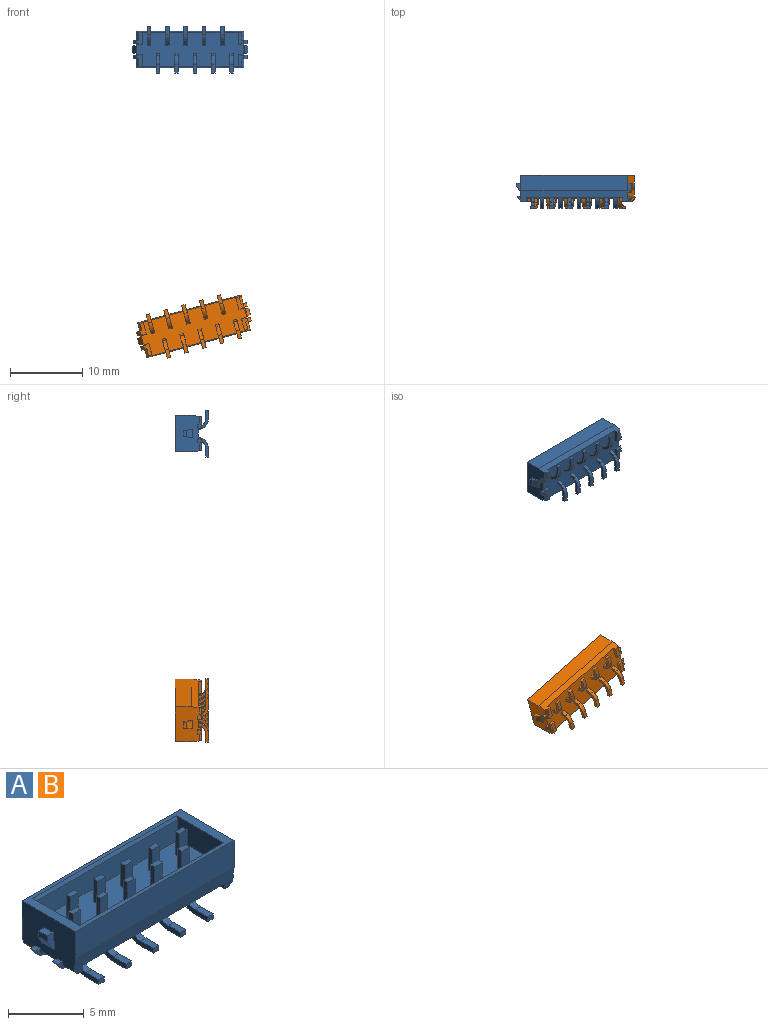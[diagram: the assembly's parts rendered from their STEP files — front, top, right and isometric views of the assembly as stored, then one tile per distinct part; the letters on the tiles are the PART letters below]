
ASSEMBLY  parts=2 mates=1
PART A: 227 faces, bbox 15.9x6.5x4.6 mm
  f0: plane 5x3.3mm, normal (-1,0,0), area 14.7mm2, adj f1,f3,f5,f6,f7,f8,f11,f14
  f1: plane 1.25x0.55mm, normal (0,0.99,0.12), area 0.5mm2, adj f0,f2,f4,f5,f6
  f2: plane 1.11x0.78mm, normal (-0.87,0,-0.5), area 0.9mm2, adj f1,f3,f4,f6
  f3: plane 1.25x0.55mm, normal (0,-0.99,0.12), area 0.5mm2, adj f0,f2,f4,f5,f6
  f4: plane 0.92x0.47mm, normal (-1,0,0), area 0.4mm2, adj f1,f2,f3,f5
  f5: plane 0.8x0.55mm, normal (0,0,1), area 0.4mm2, adj f0,f1,f3,f4
  f6: plane 1.11x0.1mm, normal (0,0,-1), area 0.1mm2, adj f0,f1,f2,f3
  f7: plane 0.5x0.45mm, normal (0,0,1), area 0.2mm2, adj f0,f11,f45,f46
  f8: plane 0.5x0.45mm, normal (0,0,1), area 0.2mm2, adj f0,f14,f112,f113
  f9: plane 0.5x0.45mm, normal (0,0,1), area 0.2mm2, adj f28,f224,f225,f226
  f10: plane 0.5x0.45mm, normal (0,0,1), area 0.2mm2, adj f21,f22,f23,f28
  f11: plane 0.75x0.6mm, normal (0,-1,0), area 0.2mm2, adj f0,f7,f13,f18,f41,f46
  f12: plane 0.54x0.5mm, normal (-0.77,0,-0.64), area 0.4mm2, adj f14,f17,f112,f113
  f13: plane 0.54x0.5mm, normal (-0.77,0,-0.64), area 0.4mm2, adj f11,f18,f45,f46
  f14: plane 0.75x0.6mm, normal (0,1,0), area 0.2mm2, adj f0,f8,f12,f17,f44,f113
  f15: plane 1.68x0.78mm, normal (0,0,-1), area 0.9mm2, adj f19,f21,f23,f24,f25,f35,f48,f51
  f16: plane 1.68x0.78mm, normal (0,0,-1), area 0.9mm2, adj f20,f26,f27,f40,f47,f49,f224,f226
  f17: plane 1.68x0.78mm, normal (0,0,-1), area 0.9mm2, adj f12,f14,f35,f36,f43,f44,f50,f112
  f18: plane 1.68x0.78mm, normal (0,0,-1), area 0.9mm2, adj f11,f13,f37,f39,f41,f42,f45,f47
  f19: plane 0.54x0.5mm, normal (0.77,0,-0.64), area 0.4mm2, adj f15,f21,f22,f23
  f20: plane 0.54x0.5mm, normal (0.77,0,-0.64), area 0.4mm2, adj f16,f224,f225,f226
  f21: plane 0.75x0.6mm, normal (0,1,0), area 0.2mm2, adj f10,f15,f19,f22,f24,f28
  f22: plane 0.5x0.06mm, normal (1,0,0), area 0mm2, adj f10,f19,f21,f23
  f23: plane 0.75x0.6mm, normal (0,-1,0), area 0.2mm2, adj f10,f15,f19,f22,f25,f28
  f24: plane 0.3x0.3mm, normal (0.71,0,-0.71), area 0.1mm2, adj f15,f21,f28,f51
  f25: plane 1.08x0.3mm, normal (0.71,0,-0.71), area 0.5mm2, adj f15,f23,f28,f35
  f26: plane 1.08x0.3mm, normal (0.71,0,-0.71), area 0.5mm2, adj f16,f28,f47,f224
  f27: plane 0.3x0.3mm, normal (0.71,0,-0.71), area 0.1mm2, adj f16,f28,f40,f226
  f28: plane 5x3.3mm, normal (1,0,0), area 14.7mm2, adj f9,f10,f21,f23,f24,f25,f26,f27
  f29: plane 1.25x0.55mm, normal (0,0.99,0.12), area 0.5mm2, adj f28,f30,f31,f33,f34
  f30: plane 1.11x0.78mm, normal (0.87,0,-0.5), area 0.9mm2, adj f29,f31,f32,f34
  f31: plane 1.11x0.1mm, normal (0,0,-1), area 0.1mm2, adj f28,f29,f30,f32
  f32: plane 1.25x0.55mm, normal (0,-0.99,0.12), area 0.5mm2, adj f28,f30,f31,f33,f34
  f33: plane 0.8x0.55mm, normal (0,0,1), area 0.4mm2, adj f28,f29,f32,f34
  f34: plane 0.92x0.47mm, normal (1,0,0), area 0.4mm2, adj f29,f30,f32,f33
  f35: plane 14.78x1.4mm, normal (0,-0.99,-0.1), area 14.7mm2, adj f0,f15,f17,f25,f28,f36,f38,f43
  f36: plane 1.73x0.45mm, normal (1,0,0), area 0.8mm2, adj f17,f35,f38,f50
  f37: plane 1.73x0.45mm, normal (1,0,0), area 0.8mm2, adj f18,f38,f39,f47
  f38: plane 14.78x4.8mm, normal (0,0,-1), area 63.6mm2, adj f0,f28,f35,f36,f37,f39,f40,f47
  f39: plane 0.78x0.45mm, normal (0,-1,0), area 0.3mm2, adj f0,f18,f37,f38,f41
  f40: plane 0.78x0.45mm, normal (0,-1,0), area 0.3mm2, adj f16,f27,f28,f38,f49
  f41: plane 0.3x0.3mm, normal (-0.71,0,-0.71), area 0.1mm2, adj f0,f11,f18,f39
  f42: plane 1.08x0.3mm, normal (-0.71,0,-0.71), area 0.5mm2, adj f0,f18,f45,f47
  f43: plane 1.08x0.3mm, normal (-0.71,0,-0.71), area 0.5mm2, adj f0,f17,f35,f112
  f44: plane 0.3x0.3mm, normal (-0.71,0,-0.71), area 0.1mm2, adj f0,f14,f17,f50
  f45: plane 0.75x0.6mm, normal (0,1,0), area 0.2mm2, adj f0,f7,f13,f18,f42,f46
  f46: plane 0.5x0.06mm, normal (-1,0,0), area 0mm2, adj f7,f11,f13,f45
  f47: plane 14.78x1.4mm, normal (0,0.99,-0.1), area 14.7mm2, adj f0,f16,f18,f26,f28,f37,f38,f42
  f48: plane 1.73x0.45mm, normal (-1,0,0), area 0.8mm2, adj f15,f35,f38,f51
  f49: plane 1.73x0.45mm, normal (-1,0,0), area 0.8mm2, adj f16,f38,f40,f47
  f50: plane 0.78x0.45mm, normal (0,1,0), area 0.3mm2, adj f0,f17,f36,f38,f44
  f51: plane 0.78x0.45mm, normal (0,1,0), area 0.3mm2, adj f15,f24,f28,f38,f48
  f52: plane 14.78x2.2mm, normal (0,1,0), area 32.5mm2, adj f0,f28,f47,f53
  f53: plane 14.78x5mm, normal (0,0,1), area 15mm2, adj f0,f28,f52,f54,f55,f58,f59,f60
  f54: plane 14.78x2.2mm, normal (0,-1,0), area 32.5mm2, adj f0,f28,f35,f53
  f55: plane 4.4x1.85mm, normal (-1,0,0), area 7.6mm2, adj f53,f56,f57,f58,f60,f61
  f56: plane 13.38x4mm, normal (0,0,1), area 50.8mm2, adj f55,f57,f59,f61,f62,f63,f64,f66
  f57: plane 13.38x1.61mm, normal (0,1,0.04), area 21.5mm2, adj f55,f56,f58,f59
  f58: plane 13.38x0.24mm, normal (0,0.87,0.5), area 3.7mm2, adj f53,f55,f57,f59
  f59: plane 4.4x1.85mm, normal (1,0,0), area 7.6mm2, adj f53,f56,f57,f58,f60,f61
  f60: plane 13.38x0.24mm, normal (0,-0.87,0.5), area 3.7mm2, adj f53,f55,f59,f61
  f61: plane 13.38x1.61mm, normal (0,-1,0.04), area 21.5mm2, adj f55,f56,f59,f60
  f62: plane 1.85x0.7mm, normal (0,1,0), area 1.3mm2, adj f56,f63,f65,f66
  f63: plane 1.85x0.39mm, normal (1,0,0), area 0.7mm2, adj f56,f62,f64,f65
  f64: plane 1.85x0.7mm, normal (0,-1,0), area 1.3mm2, adj f56,f63,f65,f66
  f65: plane 0.7x0.39mm, normal (0,0,1), area 0.3mm2, adj f62,f63,f64,f66
  f66: plane 1.85x0.39mm, normal (-1,0,0), area 0.7mm2, adj f56,f62,f64,f65
  f67: plane 1.85x0.7mm, normal (0,-1,0), area 1.3mm2, adj f56,f68,f70,f71
  f68: plane 1.85x0.39mm, normal (-1,0,0), area 0.7mm2, adj f56,f67,f69,f70
  f69: plane 1.85x0.7mm, normal (0,1,0), area 1.3mm2, adj f56,f68,f70,f71
  f70: plane 0.7x0.39mm, normal (0,0,1), area 0.3mm2, adj f67,f68,f69,f71
  f71: plane 1.85x0.39mm, normal (1,0,0), area 0.7mm2, adj f56,f67,f69,f70
  f72: plane 1.85x0.7mm, normal (0,1,0), area 1.3mm2, adj f56,f73,f75,f76
  f73: plane 1.85x0.39mm, normal (1,0,0), area 0.7mm2, adj f56,f72,f74,f75
  f74: plane 1.85x0.7mm, normal (0,-1,0), area 1.3mm2, adj f56,f73,f75,f76
  f75: plane 0.7x0.39mm, normal (0,0,1), area 0.3mm2, adj f72,f73,f74,f76
  f76: plane 1.85x0.39mm, normal (-1,0,0), area 0.7mm2, adj f56,f72,f74,f75
  f77: plane 1.85x0.7mm, normal (0,-1,0), area 1.3mm2, adj f56,f78,f80,f81
  f78: plane 1.85x0.39mm, normal (-1,0,0), area 0.7mm2, adj f56,f77,f79,f80
  f79: plane 1.85x0.7mm, normal (0,1,0), area 1.3mm2, adj f56,f78,f80,f81
  f80: plane 0.7x0.39mm, normal (0,0,1), area 0.3mm2, adj f77,f78,f79,f81
  f81: plane 1.85x0.39mm, normal (1,0,0), area 0.7mm2, adj f56,f77,f79,f80
  f82: plane 1.85x0.7mm, normal (0,1,0), area 1.3mm2, adj f56,f83,f85,f86
  f83: plane 1.85x0.39mm, normal (1,0,0), area 0.7mm2, adj f56,f82,f84,f85
  f84: plane 1.85x0.7mm, normal (0,-1,0), area 1.3mm2, adj f56,f83,f85,f86
  f85: plane 0.7x0.39mm, normal (0,0,1), area 0.3mm2, adj f82,f83,f84,f86
  f86: plane 1.85x0.39mm, normal (-1,0,0), area 0.7mm2, adj f56,f82,f84,f85
  f87: plane 1.85x0.7mm, normal (0,-1,0), area 1.3mm2, adj f56,f88,f90,f91
  f88: plane 1.85x0.39mm, normal (-1,0,0), area 0.7mm2, adj f56,f87,f89,f90
  f89: plane 1.85x0.7mm, normal (0,1,0), area 1.3mm2, adj f56,f88,f90,f91
  f90: plane 0.7x0.39mm, normal (0,0,1), area 0.3mm2, adj f87,f88,f89,f91
  f91: plane 1.85x0.39mm, normal (1,0,0), area 0.7mm2, adj f56,f87,f89,f90
  f92: plane 1.85x0.7mm, normal (0,1,0), area 1.3mm2, adj f56,f93,f95,f96
  f93: plane 1.85x0.39mm, normal (1,0,0), area 0.7mm2, adj f56,f92,f94,f95
  f94: plane 1.85x0.7mm, normal (0,-1,0), area 1.3mm2, adj f56,f93,f95,f96
  f95: plane 0.7x0.39mm, normal (0,0,1), area 0.3mm2, adj f92,f93,f94,f96
  f96: plane 1.85x0.39mm, normal (-1,0,0), area 0.7mm2, adj f56,f92,f94,f95
  f97: plane 1.85x0.7mm, normal (0,-1,0), area 1.3mm2, adj f56,f98,f100,f101
  f98: plane 1.85x0.39mm, normal (-1,0,0), area 0.7mm2, adj f56,f97,f99,f100
  f99: plane 1.85x0.7mm, normal (0,1,0), area 1.3mm2, adj f56,f98,f100,f101
  f100: plane 0.7x0.39mm, normal (0,0,1), area 0.3mm2, adj f97,f98,f99,f101
  f101: plane 1.85x0.39mm, normal (1,0,0), area 0.7mm2, adj f56,f97,f99,f100
  f102: plane 1.85x0.7mm, normal (0,1,0), area 1.3mm2, adj f56,f103,f105,f106
  f103: plane 1.85x0.39mm, normal (1,0,0), area 0.7mm2, adj f56,f102,f104,f105
  f104: plane 1.85x0.7mm, normal (0,-1,0), area 1.3mm2, adj f56,f103,f105,f106
  f105: plane 0.7x0.39mm, normal (0,0,1), area 0.3mm2, adj f102,f103,f104,f106
  f106: plane 1.85x0.39mm, normal (-1,0,0), area 0.7mm2, adj f56,f102,f104,f105
  f107: plane 1.85x0.7mm, normal (0,-1,0), area 1.3mm2, adj f56,f108,f110,f111
  f108: plane 1.85x0.39mm, normal (-1,0,0), area 0.7mm2, adj f56,f107,f109,f110
  f109: plane 1.85x0.7mm, normal (0,1,0), area 1.3mm2, adj f56,f108,f110,f111
  f110: plane 0.7x0.39mm, normal (0,0,1), area 0.3mm2, adj f107,f108,f109,f111
  f111: plane 1.85x0.39mm, normal (1,0,0), area 0.7mm2, adj f56,f107,f109,f110
  f112: plane 0.75x0.6mm, normal (0,-1,0), area 0.2mm2, adj f0,f8,f12,f17,f43,f113
  f113: plane 0.5x0.06mm, normal (-1,0,0), area 0mm2, adj f8,f12,f14,f112
  f114: plane 2.69x1.45mm, normal (-1,0,0), area 1.2mm2, adj f38,f115,f117,f118,f119,f120,f121,f122
  f115: cylinder r=1.5mm len=0.77mm, axis (1,0,0), area 0.4mm2, adj f38,f114,f116,f124
  f116: plane 2.69x1.45mm, normal (1,0,0), area 1.2mm2, adj f38,f115,f117,f118,f119,f120,f121,f122
  f117: cylinder r=1.11mm len=0.55mm, axis (1,0,0), area 0.3mm2, adj f38,f114,f116,f118
  f118: plane 0.5x0.04mm, normal (0,0.82,0.57), area 0mm2, adj f114,f116,f117,f119
  f119: cylinder r=1.11mm len=0.91mm, axis (1,0,0), area 0.5mm2, adj f114,f116,f118,f120
  f120: plane 1.17x0.5mm, normal (0,0,1), area 0.6mm2, adj f114,f116,f119,f121
  f121: plane 0.5x0.39mm, normal (0,1,0), area 0.2mm2, adj f114,f116,f120,f122
  f122: plane 1.17x0.5mm, normal (0,0,-1), area 0.6mm2, adj f114,f116,f121,f123
  f123: cylinder r=1.5mm len=1.23mm, axis (1,0,0), area 0.7mm2, adj f114,f116,f122,f124
  f124: plane 0.5x0.04mm, normal (0,-0.82,-0.57), area 0mm2, adj f114,f115,f116,f123
  f125: plane 2.69x1.45mm, normal (-1,0,0), area 1.2mm2, adj f38,f126,f128,f129,f130,f131,f132,f133
  f126: cylinder r=1.11mm len=0.55mm, axis (1,0,0), area 0.3mm2, adj f38,f125,f127,f135
  f127: plane 2.69x1.45mm, normal (1,0,0), area 1.2mm2, adj f38,f126,f128,f129,f130,f131,f132,f133
  f128: cylinder r=1.5mm len=0.77mm, axis (1,0,0), area 0.4mm2, adj f38,f125,f127,f129
  f129: plane 0.5x0.04mm, normal (0,0.82,-0.57), area 0mm2, adj f125,f127,f128,f130
  f130: cylinder r=1.5mm len=1.23mm, axis (1,0,0), area 0.7mm2, adj f125,f127,f129,f131
  f131: plane 1.17x0.5mm, normal (0,0,-1), area 0.6mm2, adj f125,f127,f130,f132
  f132: plane 0.5x0.39mm, normal (0,-1,0), area 0.2mm2, adj f125,f127,f131,f133
  f133: plane 1.17x0.5mm, normal (0,0,1), area 0.6mm2, adj f125,f127,f132,f134
  f134: cylinder r=1.11mm len=0.91mm, axis (1,0,0), area 0.5mm2, adj f125,f127,f133,f135
  f135: plane 0.5x0.04mm, normal (0,-0.82,0.57), area 0mm2, adj f125,f126,f127,f134
  f136: plane 2.69x1.45mm, normal (-1,0,0), area 1.2mm2, adj f38,f137,f139,f140,f141,f142,f143,f144
  f137: cylinder r=1.5mm len=0.77mm, axis (1,0,0), area 0.4mm2, adj f38,f136,f138,f146
  f138: plane 2.69x1.45mm, normal (1,0,0), area 1.2mm2, adj f38,f137,f139,f140,f141,f142,f143,f144
  f139: cylinder r=1.11mm len=0.55mm, axis (1,0,0), area 0.3mm2, adj f38,f136,f138,f140
  f140: plane 0.5x0.04mm, normal (0,0.82,0.57), area 0mm2, adj f136,f138,f139,f141
  f141: cylinder r=1.11mm len=0.91mm, axis (1,0,0), area 0.5mm2, adj f136,f138,f140,f142
  f142: plane 1.17x0.5mm, normal (0,0,1), area 0.6mm2, adj f136,f138,f141,f143
  f143: plane 0.5x0.39mm, normal (0,1,0), area 0.2mm2, adj f136,f138,f142,f144
  f144: plane 1.17x0.5mm, normal (0,0,-1), area 0.6mm2, adj f136,f138,f143,f145
  f145: cylinder r=1.5mm len=1.23mm, axis (1,0,0), area 0.7mm2, adj f136,f138,f144,f146
  f146: plane 0.5x0.04mm, normal (0,-0.82,-0.57), area 0mm2, adj f136,f137,f138,f145
  f147: plane 2.69x1.45mm, normal (-1,0,0), area 1.2mm2, adj f38,f148,f150,f151,f152,f153,f154,f155
  f148: cylinder r=1.11mm len=0.55mm, axis (1,0,0), area 0.3mm2, adj f38,f147,f149,f157
  f149: plane 2.69x1.45mm, normal (1,0,0), area 1.2mm2, adj f38,f148,f150,f151,f152,f153,f154,f155
  f150: cylinder r=1.5mm len=0.77mm, axis (1,0,0), area 0.4mm2, adj f38,f147,f149,f151
  f151: plane 0.5x0.04mm, normal (0,0.82,-0.57), area 0mm2, adj f147,f149,f150,f152
  f152: cylinder r=1.5mm len=1.23mm, axis (1,0,0), area 0.7mm2, adj f147,f149,f151,f153
  f153: plane 1.17x0.5mm, normal (0,0,-1), area 0.6mm2, adj f147,f149,f152,f154
  f154: plane 0.5x0.39mm, normal (0,-1,0), area 0.2mm2, adj f147,f149,f153,f155
  f155: plane 1.17x0.5mm, normal (0,0,1), area 0.6mm2, adj f147,f149,f154,f156
  f156: cylinder r=1.11mm len=0.91mm, axis (1,0,0), area 0.5mm2, adj f147,f149,f155,f157
  f157: plane 0.5x0.04mm, normal (0,-0.82,0.57), area 0mm2, adj f147,f148,f149,f156
  f158: plane 2.69x1.45mm, normal (-1,0,0), area 1.2mm2, adj f38,f159,f161,f162,f163,f164,f165,f166
  f159: cylinder r=1.5mm len=0.77mm, axis (1,0,0), area 0.4mm2, adj f38,f158,f160,f168
  f160: plane 2.69x1.45mm, normal (1,0,0), area 1.2mm2, adj f38,f159,f161,f162,f163,f164,f165,f166
  f161: cylinder r=1.11mm len=0.55mm, axis (1,0,0), area 0.3mm2, adj f38,f158,f160,f162
  f162: plane 0.5x0.04mm, normal (0,0.82,0.57), area 0mm2, adj f158,f160,f161,f163
  f163: cylinder r=1.11mm len=0.91mm, axis (1,0,0), area 0.5mm2, adj f158,f160,f162,f164
  f164: plane 1.17x0.5mm, normal (0,0,1), area 0.6mm2, adj f158,f160,f163,f165
  f165: plane 0.5x0.39mm, normal (0,1,0), area 0.2mm2, adj f158,f160,f164,f166
  f166: plane 1.17x0.5mm, normal (0,0,-1), area 0.6mm2, adj f158,f160,f165,f167
  f167: cylinder r=1.5mm len=1.23mm, axis (1,0,0), area 0.7mm2, adj f158,f160,f166,f168
  f168: plane 0.5x0.04mm, normal (0,-0.82,-0.57), area 0mm2, adj f158,f159,f160,f167
  f169: plane 2.69x1.45mm, normal (-1,0,0), area 1.2mm2, adj f38,f170,f171,f172,f173,f174,f175,f176
  f170: cylinder r=1.5mm len=0.77mm, axis (1,0,0), area 0.4mm2, adj f38,f169,f171,f179
  f171: plane 0.5x0.04mm, normal (0,0.82,-0.57), area 0mm2, adj f169,f170,f172,f179
  f172: cylinder r=1.5mm len=1.23mm, axis (1,0,0), area 0.7mm2, adj f169,f171,f173,f179
  f173: plane 1.17x0.5mm, normal (0,0,-1), area 0.6mm2, adj f169,f172,f174,f179
  f174: plane 0.5x0.39mm, normal (0,-1,0), area 0.2mm2, adj f169,f173,f175,f179
  f175: plane 1.17x0.5mm, normal (0,0,1), area 0.6mm2, adj f169,f174,f176,f179
  f176: cylinder r=1.11mm len=0.91mm, axis (1,0,0), area 0.5mm2, adj f169,f175,f177,f179
  f177: plane 0.5x0.04mm, normal (0,-0.82,0.57), area 0mm2, adj f169,f176,f178,f179
  f178: cylinder r=1.11mm len=0.55mm, axis (1,0,0), area 0.3mm2, adj f38,f169,f177,f179
  f179: plane 2.69x1.45mm, normal (1,0,0), area 1.2mm2, adj f38,f170,f171,f172,f173,f174,f175,f176
  f180: plane 2.69x1.45mm, normal (-1,0,0), area 1.2mm2, adj f38,f181,f183,f184,f185,f186,f187,f188
  f181: cylinder r=1.5mm len=0.77mm, axis (1,0,0), area 0.4mm2, adj f38,f180,f182,f190
  f182: plane 2.69x1.45mm, normal (1,0,0), area 1.2mm2, adj f38,f181,f183,f184,f185,f186,f187,f188
  f183: cylinder r=1.11mm len=0.55mm, axis (1,0,0), area 0.3mm2, adj f38,f180,f182,f184
  f184: plane 0.5x0.04mm, normal (0,0.82,0.57), area 0mm2, adj f180,f182,f183,f185
  f185: cylinder r=1.11mm len=0.91mm, axis (1,0,0), area 0.5mm2, adj f180,f182,f184,f186
  f186: plane 1.17x0.5mm, normal (0,0,1), area 0.6mm2, adj f180,f182,f185,f187
  f187: plane 0.5x0.39mm, normal (0,1,0), area 0.2mm2, adj f180,f182,f186,f188
  f188: plane 1.17x0.5mm, normal (0,0,-1), area 0.6mm2, adj f180,f182,f187,f189
  f189: cylinder r=1.5mm len=1.23mm, axis (1,0,0), area 0.7mm2, adj f180,f182,f188,f190
  f190: plane 0.5x0.04mm, normal (0,-0.82,-0.57), area 0mm2, adj f180,f181,f182,f189
  f191: plane 2.69x1.45mm, normal (-1,0,0), area 1.2mm2, adj f38,f192,f193,f194,f195,f196,f197,f198
  f192: cylinder r=1.5mm len=0.77mm, axis (1,0,0), area 0.4mm2, adj f38,f191,f193,f201
  f193: plane 0.5x0.04mm, normal (0,0.82,-0.57), area 0mm2, adj f191,f192,f194,f201
  f194: cylinder r=1.5mm len=1.23mm, axis (1,0,0), area 0.7mm2, adj f191,f193,f195,f201
  f195: plane 1.17x0.5mm, normal (0,0,-1), area 0.6mm2, adj f191,f194,f196,f201
  f196: plane 0.5x0.39mm, normal (0,-1,0), area 0.2mm2, adj f191,f195,f197,f201
  f197: plane 1.17x0.5mm, normal (0,0,1), area 0.6mm2, adj f191,f196,f198,f201
  f198: cylinder r=1.11mm len=0.91mm, axis (1,0,0), area 0.5mm2, adj f191,f197,f199,f201
  f199: plane 0.5x0.04mm, normal (0,-0.82,0.57), area 0mm2, adj f191,f198,f200,f201
  f200: cylinder r=1.11mm len=0.55mm, axis (1,0,0), area 0.3mm2, adj f38,f191,f199,f201
  f201: plane 2.69x1.45mm, normal (1,0,0), area 1.2mm2, adj f38,f192,f193,f194,f195,f196,f197,f198
  f202: plane 2.69x1.45mm, normal (-1,0,0), area 1.2mm2, adj f38,f203,f205,f206,f207,f208,f209,f210
  f203: cylinder r=1.5mm len=0.77mm, axis (1,0,0), area 0.4mm2, adj f38,f202,f204,f212
  f204: plane 2.69x1.45mm, normal (1,0,0), area 1.2mm2, adj f38,f203,f205,f206,f207,f208,f209,f210
  f205: cylinder r=1.11mm len=0.55mm, axis (1,0,0), area 0.3mm2, adj f38,f202,f204,f206
  f206: plane 0.5x0.04mm, normal (0,0.82,0.57), area 0mm2, adj f202,f204,f205,f207
  f207: cylinder r=1.11mm len=0.91mm, axis (1,0,0), area 0.5mm2, adj f202,f204,f206,f208
  f208: plane 1.17x0.5mm, normal (0,0,1), area 0.6mm2, adj f202,f204,f207,f209
  f209: plane 0.5x0.39mm, normal (0,1,0), area 0.2mm2, adj f202,f204,f208,f210
  f210: plane 1.17x0.5mm, normal (0,0,-1), area 0.6mm2, adj f202,f204,f209,f211
  f211: cylinder r=1.5mm len=1.23mm, axis (1,0,0), area 0.7mm2, adj f202,f204,f210,f212
  f212: plane 0.5x0.04mm, normal (0,-0.82,-0.57), area 0mm2, adj f202,f203,f204,f211
  f213: plane 2.69x1.45mm, normal (-1,0,0), area 1.2mm2, adj f38,f214,f215,f216,f217,f218,f219,f220
  f214: cylinder r=1.5mm len=0.77mm, axis (1,0,0), area 0.4mm2, adj f38,f213,f215,f223
  f215: plane 0.5x0.04mm, normal (0,0.82,-0.57), area 0mm2, adj f213,f214,f216,f223
  f216: cylinder r=1.5mm len=1.23mm, axis (1,0,0), area 0.7mm2, adj f213,f215,f217,f223
  f217: plane 1.17x0.5mm, normal (0,0,-1), area 0.6mm2, adj f213,f216,f218,f223
  f218: plane 0.5x0.39mm, normal (0,-1,0), area 0.2mm2, adj f213,f217,f219,f223
  f219: plane 1.17x0.5mm, normal (0,0,1), area 0.6mm2, adj f213,f218,f220,f223
  f220: cylinder r=1.11mm len=0.91mm, axis (1,0,0), area 0.5mm2, adj f213,f219,f221,f223
  f221: plane 0.5x0.04mm, normal (0,-0.82,0.57), area 0mm2, adj f213,f220,f222,f223
  f222: cylinder r=1.11mm len=0.55mm, axis (1,0,0), area 0.3mm2, adj f38,f213,f221,f223
  f223: plane 2.69x1.45mm, normal (1,0,0), area 1.2mm2, adj f38,f214,f215,f216,f217,f218,f219,f220
  f224: plane 0.75x0.6mm, normal (0,1,0), area 0.2mm2, adj f9,f16,f20,f26,f28,f225
  f225: plane 0.5x0.06mm, normal (1,0,0), area 0mm2, adj f9,f20,f224,f226
  f226: plane 0.75x0.6mm, normal (0,-1,0), area 0.2mm2, adj f9,f16,f20,f27,f28,f225
PART B: same geometry as A
PLACE A rot(axis=(0,0.71,0.71),180deg) t=(0,1.85,0)mm
PLACE B rot(axis=(-0.98,-0.13,-0.13),91deg) t=(0.51,1.85,-38.26)mm
MATE planar B.f217 <-> A.f131  axis (0,-1,0) through (-5.71,-2.75,-37.17)mm
